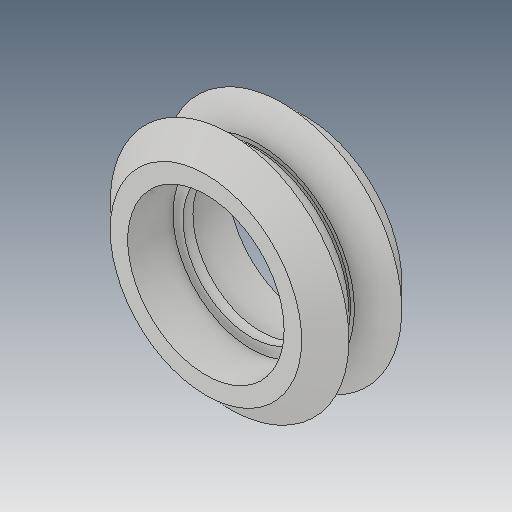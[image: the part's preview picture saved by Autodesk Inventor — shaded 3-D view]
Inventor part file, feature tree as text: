
AUTODESK INVENTOR PART (.ipt)
format: ipt  version: 2017 (Build 210142000, 142)  size: 157,184 bytes
history: native  units: mm
features: sketch x5, other x3
ambient origin geometry x8: Origin, YZ Plane, XZ Plane, XY Plane, X Axis, Y Axis, Z Axis, Center Point
bodies: Solid1 (feature_tree)
feature tree (8):
  other  "dELRIN_MIR1.ipt"
  other  "Solid1::dELRIN_MIR1.ipt"
  other  "TaggingFeature1"
  sketch  "Sketch1"  dims[d0=10.0mm]
  sketch  "Sketch2"
  sketch  "Sketch3"
  sketch  "Sketch4"
  sketch  "Sketch5"
